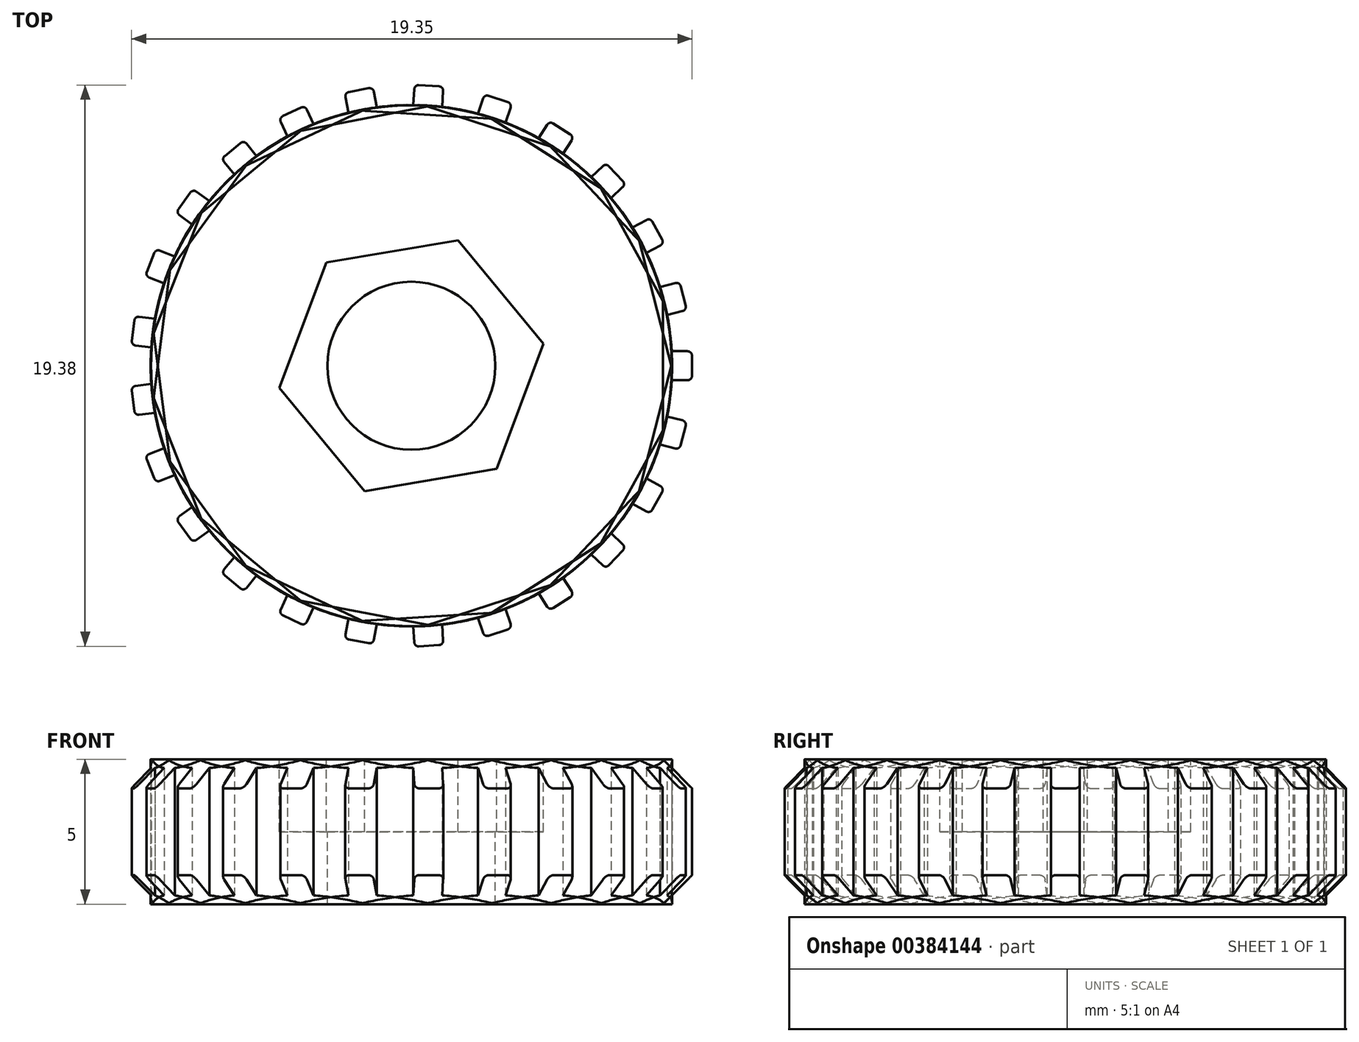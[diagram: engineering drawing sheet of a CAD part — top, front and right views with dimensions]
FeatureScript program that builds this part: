
annotation { "Feature Type Name" : "Feature", "Feature Type Description" : "" }
export const myFeature = defineFeature(function(context is Context, id is Id, definition is map)
    precondition{}
    {
        {
            var Q0;
            Q0=qCreatedBy(makeId("Top.planeOp"),FACE);
            var sketch = newSketch(context, id + "F0", { "sketchPlane" : qUnion([Q0])});
            skCircle(sketch, "E0", {"center": v(0, 0) * mm, "radius": 9 * mm});
            skPoint(sketch, "E1.middle", {"position": v(9, 0) * mm});
            skCircle(sketch, "E2", {"center": v(0, 0) * mm, "radius": 9.7 * mm, "construction": true});
            skLineSegment(sketch, "E3", {"start": v(7.52, 0.5) * mm, "end": v(11.28, 0.5) * mm, "construction": true});
            skLineSegment(sketch, "E4.MirrorCS", {"start": v(7.52, -0.5) * mm, "end": v(11.28, -0.5) * mm, "construction": true});
            skLineSegment(sketch, "E5", {"start": v(8.99, 0.5) * mm, "end": v(9.69, 0.5) * mm});
            skLineSegment(sketch, "E6", {"start": v(9.69, 0.5) * mm, "end": v(9.69, -0.5) * mm});
            skLineSegment(sketch, "E7", {"start": v(9.69, -0.5) * mm, "end": v(8.99, -0.5) * mm});
            skSolve(sketch);
        }
        {
            var Q0;
            {var subQ0=sQuery(id+"F0.wireOp",EDGE,"E0");var subQ1=makeQuery(id+"F0.imprint","INTERSECT",VERTEX,{"derivedFrom":[subQ0,sQuery(id+"F0.wireOp",EDGE,"E5")]});Q0=makeQuery(id+"F0.imprint","IMPRINT",FACE,{"disambiguationData":[TD([[makeQuery(id+"F0.imprint","IMPRINT",EDGE,{"disambiguationData":[TD([[subQ1,-1.0]])],"derivedFrom":subQ0}),1.0]])]});}
            var Q1;
            {var subQ0=sQuery(id+"F0.wireOp",EDGE,"E5");Q1=makeQuery(id+"F0.imprint","IMPRINT",FACE,{"disambiguationData":[TD([[makeQuery(id+"F0.imprint","IMPRINT",EDGE,{"derivedFrom":subQ0}),-1.0]])]});}
            extrude(context, id + "F1", {"entities" : qUnion([Q0, Q1]), "depth" : 5 * mm});
        }
        {
            var Q0;
            Q0=makeQuery(id+"F1.opExtrude","SWEPT_EDGE",EDGE,{"disambiguationData":[OSD([sQuery(id+"F0.wireOp",EDGE,"E6"),sQuery(id+"F0.wireOp",EDGE,"E7")])]});
            var Q1;
            Q1=makeQuery(id+"F1.opExtrude","SWEPT_EDGE",EDGE,{"disambiguationData":[OSD([sQuery(id+"F0.wireOp",EDGE,"E5"),sQuery(id+"F0.wireOp",EDGE,"E6")])]});
            fillet(context, id + "F2", {"entities" : qUnion([Q0, Q1]), "radius" : 0.15 * mm, "tangentPropagation" : true, "allowEdgeOverflow" : false});
        }
        {
            var Q0;
            Q0=makeQuery(id+"F1.opExtrude","CAP_EDGE",EDGE,{"disambiguationData":[OSD([sQuery(id+"F0.wireOp",EDGE,"E6")])],"isStart":true});
            var Q1;
            Q1=makeQuery(id+"F1.opExtrude","CAP_EDGE",EDGE,{"disambiguationData":[OSD([sQuery(id+"F0.wireOp",EDGE,"E6")])],"isStart":false});
            chamfer(context, id + "F3", {"entities" : qUnion([Q0, Q1]), "width" : 1 * mm, "tangentPropagation" : true});
        }
        {
            var Q0;
            Q0=makeQuery(id+"F1.opExtrude","SWEPT_BODY",BODY,{"disambiguationData":[OSD([sQuery(id+"F0.wireOp",EDGE,"E0"),sQuery(id+"F0.wireOp",EDGE,"E5"),sQuery(id+"F0.wireOp",EDGE,"E6"),sQuery(id+"F0.wireOp",EDGE,"E7")])]});
            var Q1;
            Q1=makeQuery(id+"F1.opExtrude","SWEPT_FACE",FACE,{"disambiguationData":[OSD([sQuery(id+"F0.wireOp",EDGE,"E0")])]});
            circularPattern(context, id + "F4", {"entities" : qUnion([Q0]), "axis" : qUnion([Q1]), "angle" : 360 * degree, "instanceCount" : 25, "equalSpace" : true, "computeTransformsWithoutBuiltin" : true});
        }
        {
            var Q0;
            Q0=makeQuery(id+"F1.opExtrude","CAP_FACE",FACE,{"disambiguationData":[OSD([sQuery(id+"F0.wireOp",EDGE,"E0"),sQuery(id+"F0.wireOp",EDGE,"E5"),sQuery(id+"F0.wireOp",EDGE,"E6"),sQuery(id+"F0.wireOp",EDGE,"E7")])],"isStart":false});
            var sketch = newSketch(context, id + "F5", { "sketchPlane" : qUnion([Q0])});
            skCircle(sketch, "E8", {"center": v(0, 0) * mm, "radius": 2.9 * mm});
            skCircle(sketch, "E9.cCircle", {"center": v(0, 0) * mm, "radius": 4 * mm, "construction": true});
            skLineSegment(sketch, "E9.0", {"start": v(4.55, 0.77) * mm, "end": v(2.94, -3.56) * mm});
            skLineSegment(sketch, "E9.1", {"start": v(2.94, -3.56) * mm, "end": v(-1.61, -4.33) * mm});
            skLineSegment(sketch, "E9.2", {"start": v(-1.61, -4.33) * mm, "end": v(-4.55, -0.77) * mm});
            skLineSegment(sketch, "E9.3", {"start": v(-4.55, -0.77) * mm, "end": v(-2.94, 3.56) * mm});
            skLineSegment(sketch, "E9.4", {"start": v(-2.94, 3.56) * mm, "end": v(1.61, 4.33) * mm});
            skLineSegment(sketch, "E9.5", {"start": v(1.61, 4.33) * mm, "end": v(4.55, 0.77) * mm});
            skPoint(sketch, "E9.0.midPoint", {"position": v(3.75, -1.4) * mm});
            skSolve(sketch);
        }
        {
            var Q0;
            Q0=makeQuery(id+"F5.imprint","IMPRINT",FACE,{"disambiguationData":[TD([[makeQuery(id+"F5.imprint","IMPRINT",EDGE,{"derivedFrom":sQuery(id+"F5.wireOp",EDGE,"E8")}),1.0]])]});
            extrude(context, id + "F6", {"entities" : qUnion([Q0]), "operationType" : NewBodyOperationType.REMOVE, "endBound" : BoundingType.THROUGH_ALL, "oppositeDirection" : true, "depth" : 25 * mm});
        }
        {
            var Q0;
            Q0=makeQuery(id+"F5.imprint","IMPRINT",FACE,{"disambiguationData":[TD([[makeQuery(id+"F5.imprint","IMPRINT",EDGE,{"derivedFrom":sQuery(id+"F5.wireOp",EDGE,"E8")}),-1.0]])]});
            extrude(context, id + "F7", {"entities" : qUnion([Q0]), "operationType" : NewBodyOperationType.REMOVE, "oppositeDirection" : true, "depth" : 2.5 * mm});
        }
    });
